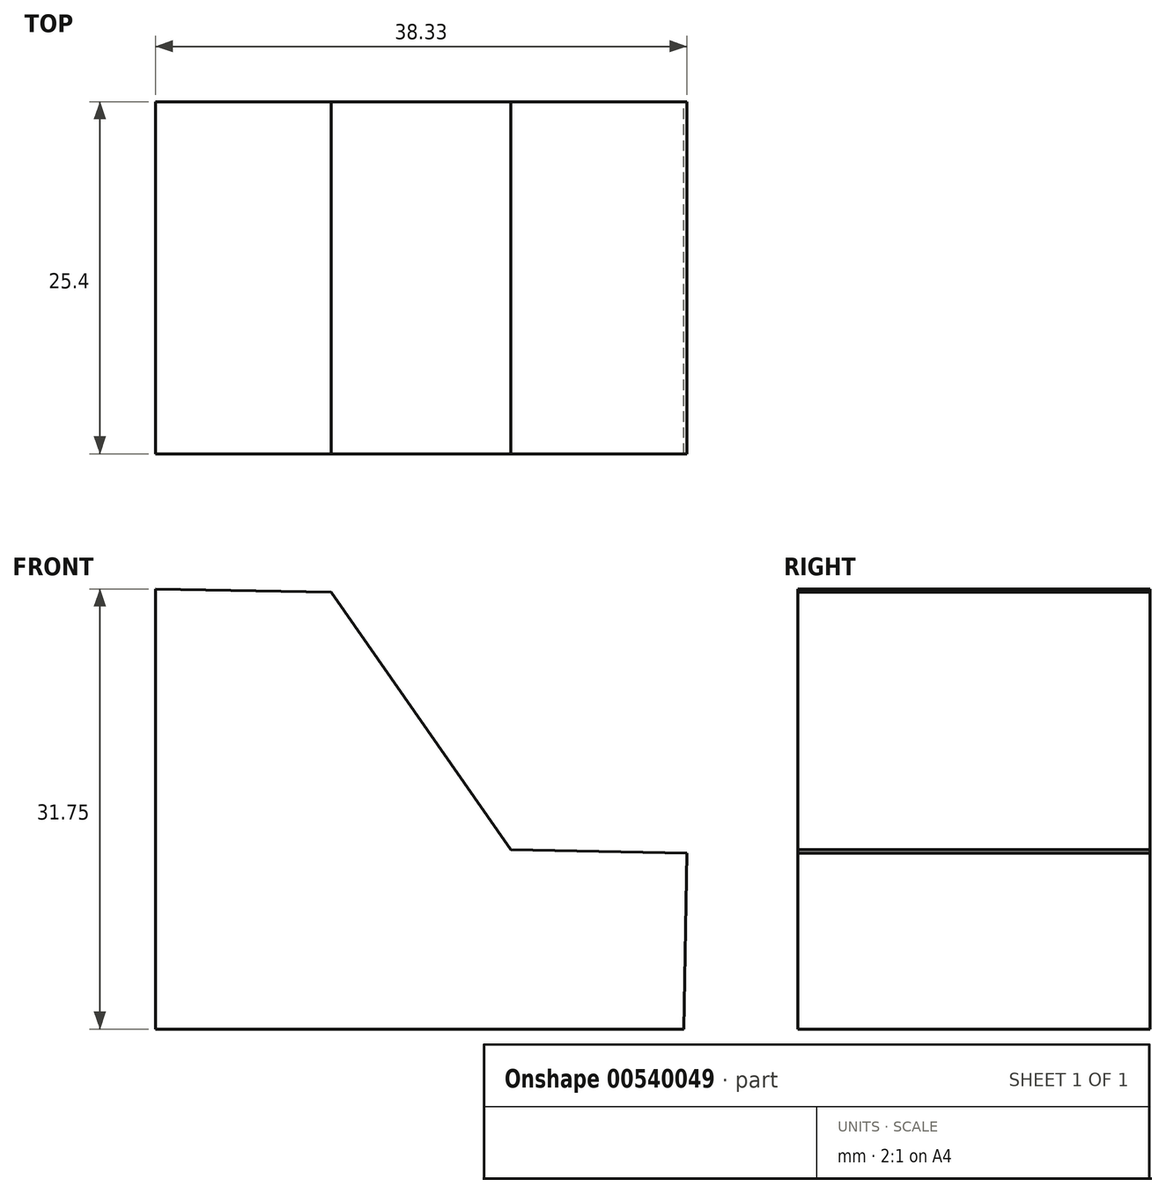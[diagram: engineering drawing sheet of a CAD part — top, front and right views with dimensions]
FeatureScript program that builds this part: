
annotation { "Feature Type Name" : "Feature", "Feature Type Description" : "" }
export const myFeature = defineFeature(function(context is Context, id is Id, definition is map)
    precondition{}
    {
        {
            var Q0;
            Q0=qCreatedBy(makeId("Front.planeOp"),FACE);
            var sketch = newSketch(context, id + "F0", { "sketchPlane" : qUnion([Q0])});
            skLineSegment(sketch, "E0", {"start": v(-38.33, 40.47) * mm, "end": v(-38.33, 8.72) * mm});
            skLineSegment(sketch, "E1", {"start": v(-38.33, 8.72) * mm, "end": v(-0.23, 8.72) * mm});
            skLineSegment(sketch, "E2", {"start": v(-0.23, 8.72) * mm, "end": v(0, 21.41) * mm});
            skLineSegment(sketch, "E3", {"start": v(0, 21.41) * mm, "end": v(-12.7, 21.65) * mm});
            skLineSegment(sketch, "E4", {"start": v(-12.7, 21.65) * mm, "end": v(0, 21.41) * mm});
            skLineSegment(sketch, "E5", {"start": v(-0.23, 8.72) * mm, "end": v(-38.33, 8.72) * mm});
            skLineSegment(sketch, "E6", {"start": v(-38.33, 40.47) * mm, "end": v(-25.64, 40.23) * mm});
            skLineSegment(sketch, "E7", {"start": v(-25.64, 40.23) * mm, "end": v(-12.7, 21.65) * mm});
            skSolve(sketch);
        }
        {
            var Q0;
            Q0 = qSketchRegion(id + "F0", true);
            extrude(context, id + "F1", {"entities" : qUnion([Q0]), "depth" : 25.4 * mm, "offsetDistance" : 25.4 * mm});
        }
    });
